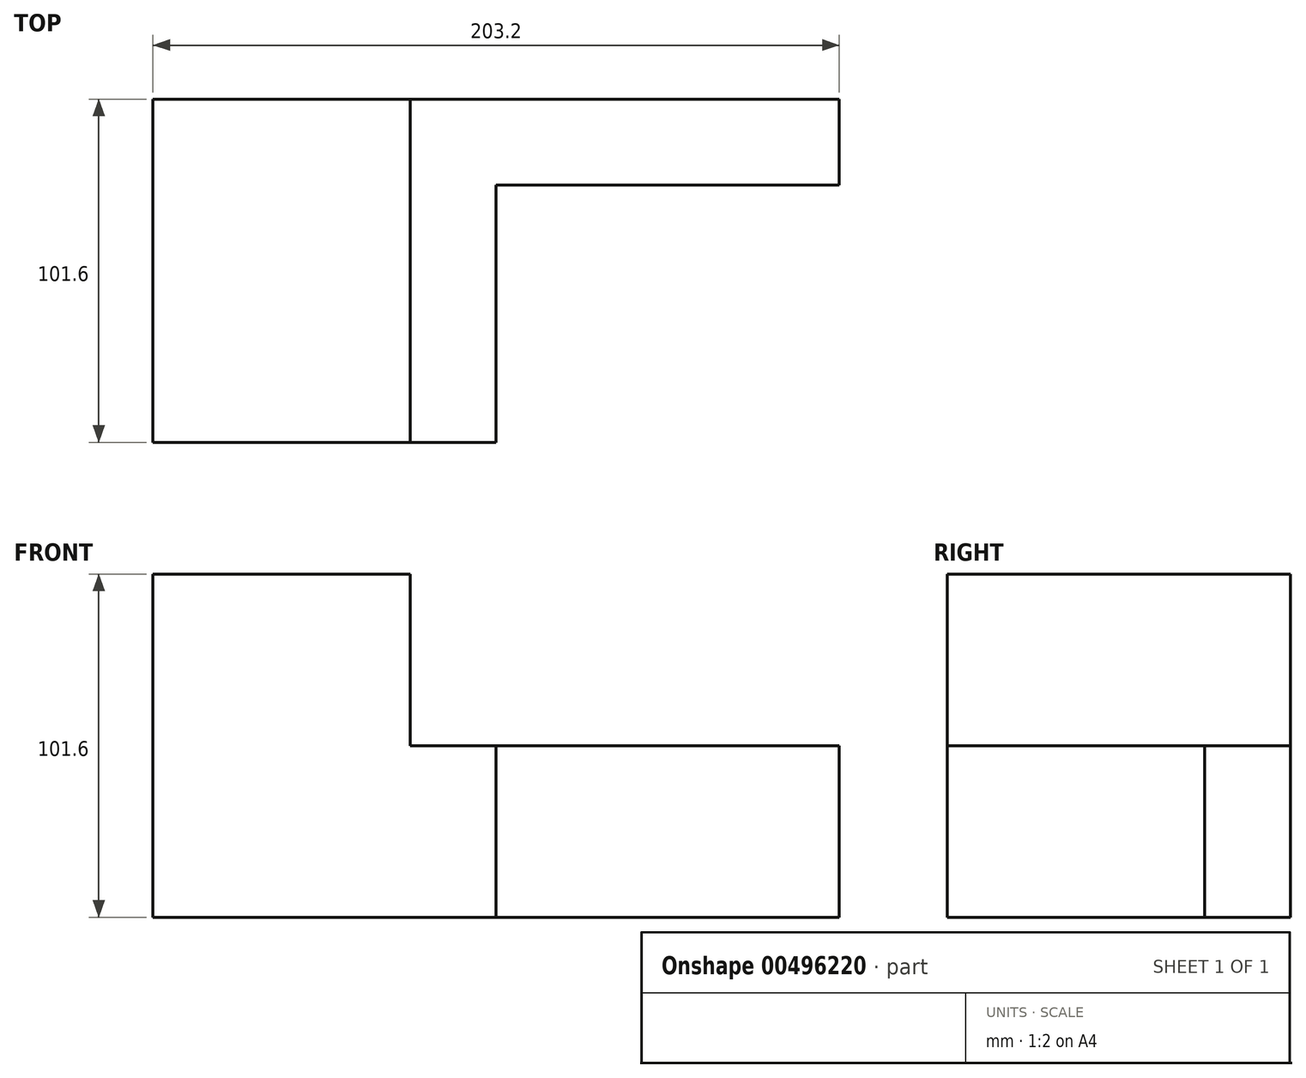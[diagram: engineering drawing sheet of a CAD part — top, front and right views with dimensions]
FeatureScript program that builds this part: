
annotation { "Feature Type Name" : "Feature", "Feature Type Description" : "" }
export const myFeature = defineFeature(function(context is Context, id is Id, definition is map)
    precondition{}
    {
        {
            var Q0;
            Q0=qCreatedBy(makeId("Top.planeOp"),FACE);
            var sketch = newSketch(context, id + "F0", { "sketchPlane" : qUnion([Q0])});
            skLineSegment(sketch, "E0.bottom", {"start": v(-74.53, 0) * mm, "end": v(128.67, 0) * mm});
            skLineSegment(sketch, "E0.top", {"start": v(-74.53, 101.6) * mm, "end": v(128.67, 101.6) * mm});
            skLineSegment(sketch, "E0.left", {"start": v(-74.53, 0) * mm, "end": v(-74.53, 101.6) * mm});
            skLineSegment(sketch, "E0.right", {"start": v(128.67, 0) * mm, "end": v(128.67, 101.6) * mm});
            skSolve(sketch);
        }
        {
            var Q0;
            Q0=qSketchRegion(id+"F0",true);
            var Q1;
            Q1=makeQuery(id+"F0.imprint","IMPRINT",FACE,{"disambiguationData":[TD([[makeQuery(id+"F0.imprint","IMPRINT",EDGE,{"derivedFrom":sQuery(id+"F0.wireOp",EDGE,"E0.bottom")}),1.0]])]});
            extrude(context, id + "F1", {"entities" : qUnion([Q0, Q1]), "depth" : 101.6 * mm});
        }
        {
            var Q0;
            Q0=makeQuery(id+"F1.opExtrude","SWEPT_FACE",FACE,{"disambiguationData":[OSD([sQuery(id+"F0.wireOp",EDGE,"E0.bottom")])]});
            var sketch = newSketch(context, id + "F2", { "sketchPlane" : qUnion([Q0])});
            skLineSegment(sketch, "E1.bottom", {"start": v(1.67, 101.6) * mm, "end": v(128.67, 101.6) * mm});
            skLineSegment(sketch, "E1.top", {"start": v(1.67, 50.8) * mm, "end": v(128.67, 50.8) * mm});
            skLineSegment(sketch, "E1.left", {"start": v(1.67, 101.6) * mm, "end": v(1.67, 50.8) * mm});
            skLineSegment(sketch, "E1.right", {"start": v(128.67, 101.6) * mm, "end": v(128.67, 50.8) * mm});
            skSolve(sketch);
        }
        {
            var Q0;
            Q0=qSketchRegion(id+"F2",true);
            extrude(context, id + "F3", {"entities" : qUnion([Q0]), "operationType" : NewBodyOperationType.REMOVE, "endBound" : BoundingType.UP_TO_NEXT, "oppositeDirection" : true, "depth" : 25.4 * mm});
        }
        {
            var Q0;
            Q0=makeQuery(id+"F3.boolean.opBoolean","COPY",FACE,{"derivedFrom":makeQuery(id+"F3.opExtrude","SWEPT_FACE",FACE,{"disambiguationData":[OSD([sQuery(id+"F2.wireOp",EDGE,"E1.top")])]})});
            var sketch = newSketch(context, id + "F4", { "sketchPlane" : qUnion([Q0])});
            skLineSegment(sketch, "E2.bottom", {"start": v(27.07, 0) * mm, "end": v(128.67, 0) * mm});
            skLineSegment(sketch, "E2.top", {"start": v(27.07, 76.2) * mm, "end": v(128.67, 76.2) * mm});
            skLineSegment(sketch, "E2.left", {"start": v(27.07, 0) * mm, "end": v(27.07, 76.2) * mm});
            skLineSegment(sketch, "E2.right", {"start": v(128.67, 0) * mm, "end": v(128.67, 76.2) * mm});
            skSolve(sketch);
        }
        {
            var Q0;
            Q0=makeQuery(id+"F4.imprint","IMPRINT",FACE,{"disambiguationData":[TD([[makeQuery(id+"F4.imprint","IMPRINT",EDGE,{"derivedFrom":sQuery(id+"F4.wireOp",EDGE,"E2.bottom")}),1.0]])]});
            extrude(context, id + "F5", {"entities" : qUnion([Q0]), "operationType" : NewBodyOperationType.REMOVE, "endBound" : BoundingType.UP_TO_NEXT, "oppositeDirection" : true, "depth" : 25.4 * mm});
        }
    });
